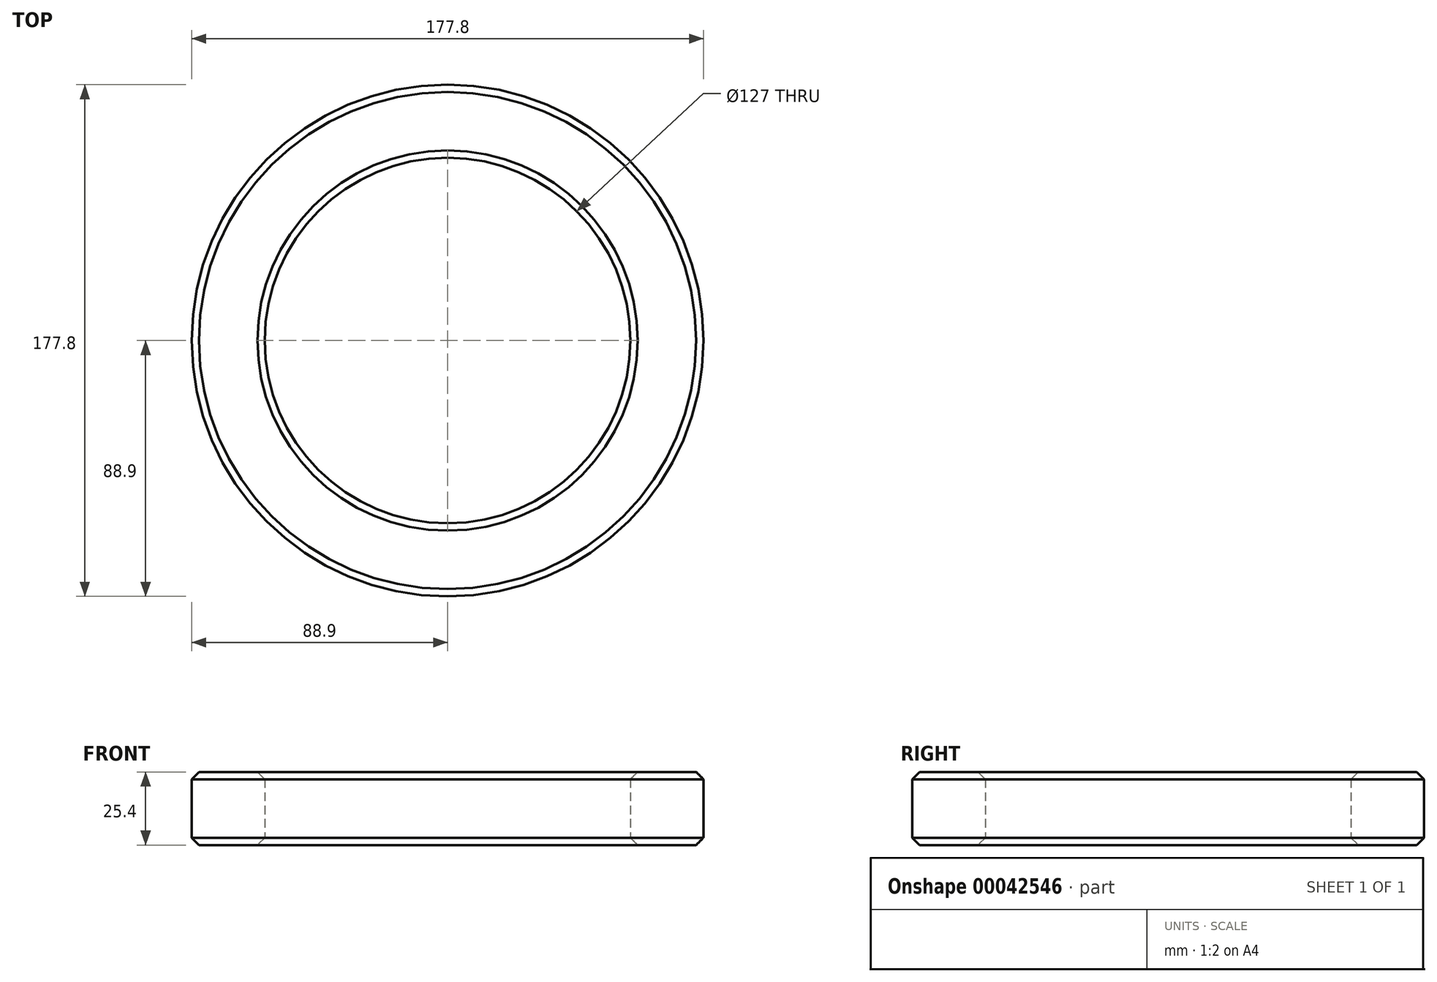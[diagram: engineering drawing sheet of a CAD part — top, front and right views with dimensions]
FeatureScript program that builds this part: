
annotation { "Feature Type Name" : "Feature", "Feature Type Description" : "" }
export const myFeature = defineFeature(function(context is Context, id is Id, definition is map)
    precondition{}
    {
        {
            var Q0;
            Q0=qCreatedBy(makeId("Top.planeOp"),FACE);
            var sketch = newSketch(context, id + "F0", { "sketchPlane" : qUnion([Q0])});
            skCircle(sketch, "E0", {"center": v(0, 0) * mm, "radius": 88.9 * mm});
            skCircle(sketch, "E1", {"center": v(0, 0) * mm, "radius": 63.5 * mm});
            skSolve(sketch);
        }
        {
            var Q0;
            Q0=makeQuery(id+"F0.imprint","IMPRINT",FACE,{"disambiguationData":[TD([[makeQuery(id+"F0.imprint","IMPRINT",EDGE,{"derivedFrom":sQuery(id+"F0.wireOp",EDGE,"E0")}),1.0]])]});
            extrude(context, id + "F1", {"entities" : qUnion([Q0]), "depth" : 12.7 * mm});
        }
        {
            var Q0;
            Q0=makeQuery(id+"F1.opExtrude","CAP_FACE",FACE,{"disambiguationData":[OSD([sQuery(id+"F0.wireOp",EDGE,"E0"),sQuery(id+"F0.wireOp",EDGE,"E1")])],"isStart":false});
            chamfer(context, id + "F2", {"entities" : qUnion([Q0]), "width" : 2.54 * mm, "tangentPropagation" : true});
        }
        {
            var Q0;
            Q0=makeQuery(id+"F1.opExtrude","SWEPT_BODY",BODY,{"disambiguationData":[OSD([sQuery(id+"F0.wireOp",EDGE,"E0"),sQuery(id+"F0.wireOp",EDGE,"E1")])]});
            var Q1;
            Q1=makeQuery(id+"F1.opExtrude","CAP_FACE",FACE,{"disambiguationData":[OSD([sQuery(id+"F0.wireOp",EDGE,"E0"),sQuery(id+"F0.wireOp",EDGE,"E1")])],"isStart":true});
            mirror(context, id + "F3", {"operationType" : NewBodyOperationType.ADD, "entities" : qUnion([Q0]), "mirrorPlane" : qUnion([Q1])});
        }
    });
